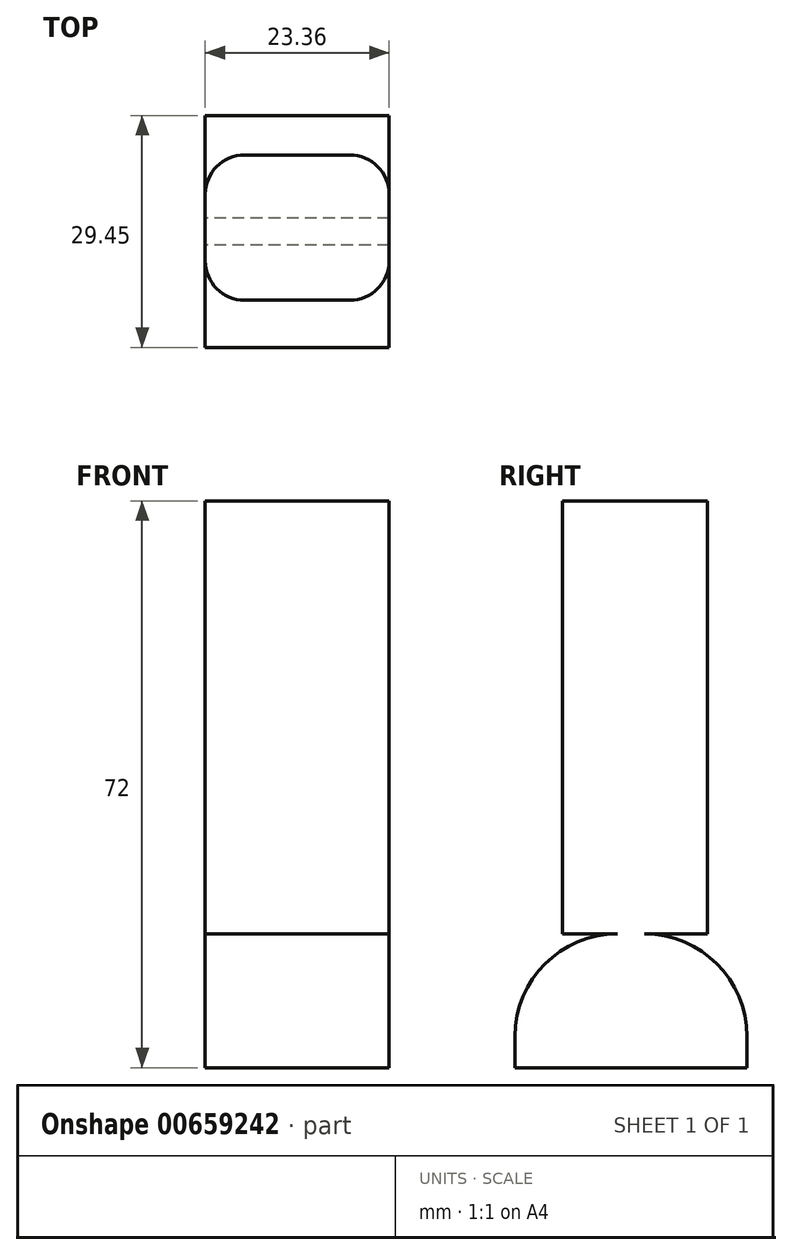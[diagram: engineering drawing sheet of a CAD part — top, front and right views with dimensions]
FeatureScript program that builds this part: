
annotation { "Feature Type Name" : "Feature", "Feature Type Description" : "" }
export const myFeature = defineFeature(function(context is Context, id is Id, definition is map)
    precondition{}
    {
        {
            var Q0;
            Q0=qCreatedBy(makeId("Top.planeOp"),FACE);
            var sketch = newSketch(context, id + "F0", { "sketchPlane" : qUnion([Q0])});
            skLineSegment(sketch, "E0.bottom", {"start": v(-39.05, -38.05) * mm, "end": v(-62.41, -38.05) * mm});
            skLineSegment(sketch, "E0.top", {"start": v(-39.05, -8.6) * mm, "end": v(-62.41, -8.6) * mm});
            skLineSegment(sketch, "E0.left", {"start": v(-39.05, -38.05) * mm, "end": v(-39.05, -8.6) * mm});
            skLineSegment(sketch, "E0.right", {"start": v(-62.41, -38.05) * mm, "end": v(-62.41, -8.6) * mm});
            skPoint(sketch, "E0.middle", {"position": v(-50.73, -23.33) * mm});
            skSolve(sketch);
        }
        {
            var Q0;
            Q0 = qSketchRegion(id + "F0", true);
            extrude(context, id + "F1", {"entities" : qUnion([Q0]), "depth" : 17 * mm, "offsetDistance" : 25 * mm});
        }
        {
            var Q0;
            Q0=makeQuery(id+"F1.opExtrude","CAP_EDGE",EDGE,{"disambiguationData":[OSD([sQuery(id+"F0.wireOp",EDGE,"E0.bottom")])],"isStart":false});
            var Q1;
            Q1=makeQuery(id+"F1.opExtrude","CAP_EDGE",EDGE,{"disambiguationData":[OSD([sQuery(id+"F0.wireOp",EDGE,"E0.top")])],"isStart":false});
            fillet(context, id + "F2", {"entities" : qUnion([Q0, Q1]), "radius" : 13 * mm, "tangentPropagation" : true, "allowEdgeOverflow" : false});
        }
        {
            var Q0;
            Q0=makeQuery(id+"F1.opExtrude","CAP_FACE",FACE,{"disambiguationData":[OSD([sQuery(id+"F0.wireOp",EDGE,"E0.bottom"),sQuery(id+"F0.wireOp",EDGE,"E0.top"),sQuery(id+"F0.wireOp",EDGE,"E0.left"),sQuery(id+"F0.wireOp",EDGE,"E0.right")])],"isStart":false});
            extrude(context, id + "F3", {"entities" : qUnion([Q0]), "operationType" : NewBodyOperationType.ADD, "depth" : 55 * mm, "offsetDistance" : 25 * mm});
        }
        {
            var Q0;
            {var subQ0=sQuery(id+"F0.wireOp",EDGE,"E0.right");var subQ1=sQuery(id+"F0.wireOp",EDGE,"E0.left");var subQ2=sQuery(id+"F0.wireOp",EDGE,"E0.top");var subQ3=sQuery(id+"F0.wireOp",EDGE,"E0.bottom");Q0=makeQuery(id+"F3.opExtrude","SWEPT_FACE",FACE,{"disambiguationData":[OSD([subQ3,subQ2,subQ1,subQ0]),TDD([makeQuery(id+"F2.opFillet","BLEND_EDGE",EDGE,{"blendedFrom":[makeQuery(id+"F1.opExtrude","CAP_EDGE",EDGE,{"disambiguationData":[OSD([subQ2])],"isStart":false}),makeQuery(id+"F1.opExtrude","CAP_FACE",FACE,{"disambiguationData":[OSD([subQ3,subQ2,subQ1,subQ0])],"isStart":false})],"blendedInto":[makeQuery(id+"F1.opExtrude","CAP_FACE",FACE,{"disambiguationData":[OSD([subQ3,subQ2,subQ1,subQ0])],"isStart":false})]})])]});}
            extrude(context, id + "F4", {"entities" : qUnion([Q0]), "operationType" : NewBodyOperationType.ADD, "depth" : 8 * mm, "offsetDistance" : 25 * mm});
        }
        {
            var Q0;
            {var subQ0=sQuery(id+"F0.wireOp",EDGE,"E0.right");var subQ1=sQuery(id+"F0.wireOp",EDGE,"E0.left");var subQ2=sQuery(id+"F0.wireOp",EDGE,"E0.top");var subQ3=sQuery(id+"F0.wireOp",EDGE,"E0.bottom");Q0=makeQuery(id+"F3.opExtrude","SWEPT_FACE",FACE,{"disambiguationData":[OSD([subQ3,subQ2,subQ1,subQ0]),TDD([makeQuery(id+"F2.opFillet","BLEND_EDGE",EDGE,{"blendedFrom":[makeQuery(id+"F1.opExtrude","CAP_EDGE",EDGE,{"disambiguationData":[OSD([subQ3])],"isStart":false}),makeQuery(id+"F1.opExtrude","CAP_FACE",FACE,{"disambiguationData":[OSD([subQ3,subQ2,subQ1,subQ0])],"isStart":false})],"blendedInto":[makeQuery(id+"F1.opExtrude","CAP_FACE",FACE,{"disambiguationData":[OSD([subQ3,subQ2,subQ1,subQ0])],"isStart":false})]})])]});}
            extrude(context, id + "F5", {"entities" : qUnion([Q0]), "operationType" : NewBodyOperationType.ADD, "depth" : 7 * mm, "offsetDistance" : 25 * mm});
        }
        {
            var Q0;
            {var subQ0=sQuery(id+"F0.wireOp",EDGE,"E0.left");var subQ1=sQuery(id+"F0.wireOp",EDGE,"E0.right");var subQ2=sQuery(id+"F0.wireOp",EDGE,"E0.top");var subQ3=sQuery(id+"F0.wireOp",EDGE,"E0.bottom");Q0=makeQuery(id+"F5.opExtrude","CAP_EDGE",EDGE,{"disambiguationData":[OSD([subQ3,subQ2,subQ0,subQ1]),TDD([makeQuery(id+"F3.opExtrude","SWEPT_EDGE",EDGE,{"disambiguationData":[OSD([subQ3,subQ2,subQ0,subQ1]),TDD([makeQuery(id+"F2.opFillet","BLEND_VERTEX",VERTEX,{"blendedFrom":[makeQuery(id+"F1.opExtrude","CAP_EDGE",EDGE,{"disambiguationData":[OSD([subQ3])],"isStart":false}),makeQuery(id+"F1.opExtrude","CAP_FACE",FACE,{"disambiguationData":[OSD([subQ3,subQ2,subQ0,subQ1])],"isStart":false}),makeQuery(id+"F1.opExtrude","SWEPT_FACE",FACE,{"disambiguationData":[OSD([subQ0])]})],"blendedInto":[makeQuery(id+"F1.opExtrude","CAP_FACE",FACE,{"disambiguationData":[OSD([subQ3,subQ2,subQ0,subQ1])],"isStart":false}),makeQuery(id+"F1.opExtrude","SWEPT_FACE",FACE,{"disambiguationData":[OSD([subQ0])]})]})])]})])],"isStart":false});}
            fillet(context, id + "F6", {"entities" : qUnion([Q0]), "radius" : 5 * mm, "tangentPropagation" : true, "allowEdgeOverflow" : false});
        }
        {
            var Q0;
            {var subQ0=sQuery(id+"F0.wireOp",EDGE,"E0.left");var subQ1=sQuery(id+"F0.wireOp",EDGE,"E0.right");var subQ2=sQuery(id+"F0.wireOp",EDGE,"E0.top");var subQ3=sQuery(id+"F0.wireOp",EDGE,"E0.bottom");Q0=makeQuery(id+"F4.opExtrude","CAP_EDGE",EDGE,{"disambiguationData":[OSD([subQ3,subQ2,subQ0,subQ1]),TDD([makeQuery(id+"F3.opExtrude","SWEPT_EDGE",EDGE,{"disambiguationData":[OSD([subQ3,subQ2,subQ0,subQ1]),TDD([makeQuery(id+"F2.opFillet","BLEND_VERTEX",VERTEX,{"blendedFrom":[makeQuery(id+"F1.opExtrude","CAP_EDGE",EDGE,{"disambiguationData":[OSD([subQ2])],"isStart":false}),makeQuery(id+"F1.opExtrude","CAP_FACE",FACE,{"disambiguationData":[OSD([subQ3,subQ2,subQ0,subQ1])],"isStart":false}),makeQuery(id+"F1.opExtrude","SWEPT_FACE",FACE,{"disambiguationData":[OSD([subQ0])]})],"blendedInto":[makeQuery(id+"F1.opExtrude","CAP_FACE",FACE,{"disambiguationData":[OSD([subQ3,subQ2,subQ0,subQ1])],"isStart":false}),makeQuery(id+"F1.opExtrude","SWEPT_FACE",FACE,{"disambiguationData":[OSD([subQ0])]})]})])]})])],"isStart":false});}
            fillet(context, id + "F7", {"entities" : qUnion([Q0]), "radius" : 5 * mm, "tangentPropagation" : true, "allowEdgeOverflow" : false});
        }
        {
            var Q0;
            {var subQ0=sQuery(id+"F0.wireOp",EDGE,"E0.right");var subQ1=sQuery(id+"F0.wireOp",EDGE,"E0.left");var subQ2=sQuery(id+"F0.wireOp",EDGE,"E0.top");var subQ3=sQuery(id+"F0.wireOp",EDGE,"E0.bottom");Q0=makeQuery(id+"F5.opExtrude","CAP_EDGE",EDGE,{"disambiguationData":[OSD([subQ3,subQ2,subQ1,subQ0]),TDD([makeQuery(id+"F3.opExtrude","SWEPT_EDGE",EDGE,{"disambiguationData":[OSD([subQ3,subQ2,subQ1,subQ0]),TDD([makeQuery(id+"F2.opFillet","BLEND_VERTEX",VERTEX,{"blendedFrom":[makeQuery(id+"F1.opExtrude","CAP_EDGE",EDGE,{"disambiguationData":[OSD([subQ3])],"isStart":false}),makeQuery(id+"F1.opExtrude","CAP_FACE",FACE,{"disambiguationData":[OSD([subQ3,subQ2,subQ1,subQ0])],"isStart":false}),makeQuery(id+"F1.opExtrude","SWEPT_FACE",FACE,{"disambiguationData":[OSD([subQ0])]})],"blendedInto":[makeQuery(id+"F1.opExtrude","CAP_FACE",FACE,{"disambiguationData":[OSD([subQ3,subQ2,subQ1,subQ0])],"isStart":false}),makeQuery(id+"F1.opExtrude","SWEPT_FACE",FACE,{"disambiguationData":[OSD([subQ0])]})]})])]})])],"isStart":false});}
            fillet(context, id + "F8", {"entities" : qUnion([Q0]), "radius" : 5 * mm, "tangentPropagation" : true, "allowEdgeOverflow" : false});
        }
        {
            var Q0;
            {var subQ0=sQuery(id+"F0.wireOp",EDGE,"E0.right");var subQ1=sQuery(id+"F0.wireOp",EDGE,"E0.left");var subQ2=sQuery(id+"F0.wireOp",EDGE,"E0.top");var subQ3=sQuery(id+"F0.wireOp",EDGE,"E0.bottom");Q0=makeQuery(id+"F7.opFillet","BLEND_EDGE",EDGE,{"blendedFrom":[makeQuery(id+"F4.opExtrude","CAP_EDGE",EDGE,{"disambiguationData":[OSD([subQ3,subQ2,subQ1,subQ0]),TDD([makeQuery(id+"F3.opExtrude","SWEPT_EDGE",EDGE,{"disambiguationData":[OSD([subQ3,subQ2,subQ1,subQ0]),TDD([makeQuery(id+"F2.opFillet","BLEND_VERTEX",VERTEX,{"blendedFrom":[makeQuery(id+"F1.opExtrude","CAP_EDGE",EDGE,{"disambiguationData":[OSD([subQ2])],"isStart":false}),makeQuery(id+"F1.opExtrude","CAP_FACE",FACE,{"disambiguationData":[OSD([subQ3,subQ2,subQ1,subQ0])],"isStart":false}),makeQuery(id+"F1.opExtrude","SWEPT_FACE",FACE,{"disambiguationData":[OSD([subQ1])]})],"blendedInto":[makeQuery(id+"F1.opExtrude","CAP_FACE",FACE,{"disambiguationData":[OSD([subQ3,subQ2,subQ1,subQ0])],"isStart":false}),makeQuery(id+"F1.opExtrude","SWEPT_FACE",FACE,{"disambiguationData":[OSD([subQ1])]})]})])]})])],"isStart":false}),makeQuery(id+"F4.opExtrude","CAP_FACE",FACE,{"disambiguationData":[OSD([subQ3,subQ2,subQ1,subQ0])],"isStart":false})],"blendedInto":[makeQuery(id+"F4.opExtrude","CAP_FACE",FACE,{"disambiguationData":[OSD([subQ3,subQ2,subQ1,subQ0])],"isStart":false})]});}
            var Q1;
            {var subQ0=sQuery(id+"F0.wireOp",EDGE,"E0.right");var subQ1=sQuery(id+"F0.wireOp",EDGE,"E0.left");var subQ2=sQuery(id+"F0.wireOp",EDGE,"E0.top");var subQ3=sQuery(id+"F0.wireOp",EDGE,"E0.bottom");Q1=makeQuery(id+"F4.opExtrude","CAP_EDGE",EDGE,{"disambiguationData":[OSD([subQ3,subQ2,subQ1,subQ0]),TDD([makeQuery(id+"F3.opExtrude","SWEPT_EDGE",EDGE,{"disambiguationData":[OSD([subQ3,subQ2,subQ1,subQ0]),TDD([makeQuery(id+"F2.opFillet","BLEND_VERTEX",VERTEX,{"blendedFrom":[makeQuery(id+"F1.opExtrude","CAP_EDGE",EDGE,{"disambiguationData":[OSD([subQ2])],"isStart":false}),makeQuery(id+"F1.opExtrude","CAP_FACE",FACE,{"disambiguationData":[OSD([subQ3,subQ2,subQ1,subQ0])],"isStart":false}),makeQuery(id+"F1.opExtrude","SWEPT_FACE",FACE,{"disambiguationData":[OSD([subQ0])]})],"blendedInto":[makeQuery(id+"F1.opExtrude","CAP_FACE",FACE,{"disambiguationData":[OSD([subQ3,subQ2,subQ1,subQ0])],"isStart":false}),makeQuery(id+"F1.opExtrude","SWEPT_FACE",FACE,{"disambiguationData":[OSD([subQ0])]})]})])]})])],"isStart":false});}
            fillet(context, id + "F9", {"entities" : qUnion([Q0, Q1]), "radius" : 5 * mm, "tangentPropagation" : true, "allowEdgeOverflow" : false});
        }
    });
